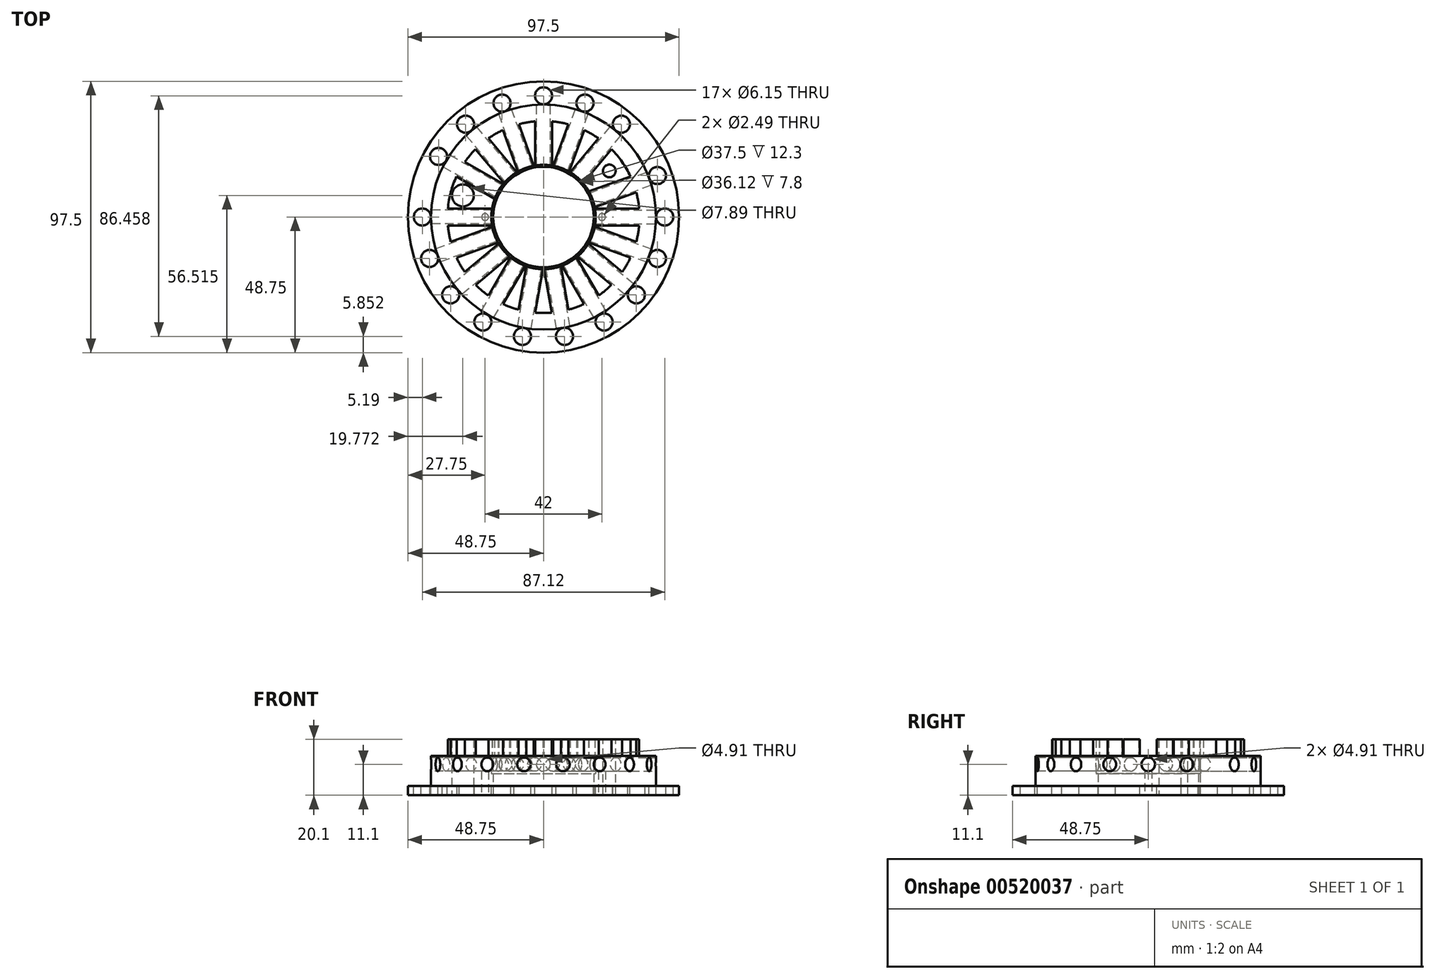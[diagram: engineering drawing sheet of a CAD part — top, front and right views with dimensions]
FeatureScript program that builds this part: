
annotation { "Feature Type Name" : "Feature", "Feature Type Description" : "" }
export const myFeature = defineFeature(function(context is Context, id is Id, definition is map)
    precondition{}
    {
        {
            var Q0;
            Q0=qCreatedBy(makeId("Front.planeOp"),FACE);
            var sketch = newSketch(context, id + "F0", { "sketchPlane" : qUnion([Q0])});
            skLineSegment(sketch, "E0", {"start": v(6.02, 0) * mm, "end": v(16.25, 0) * mm});
            skLineSegment(sketch, "E1", {"start": v(16.25, 0) * mm, "end": v(16.25, 1.1) * mm});
            skLineSegment(sketch, "E2", {"start": v(16.25, 1.1) * mm, "end": v(13.48, 1.1) * mm});
            skLineSegment(sketch, "E3", {"start": v(13.48, 1.1) * mm, "end": v(13.48, 4.7) * mm});
            skLineSegment(sketch, "E4", {"start": v(13.48, 4.7) * mm, "end": v(11.5, 4.7) * mm});
            skLineSegment(sketch, "E5", {"start": v(11.5, 4.7) * mm, "end": v(11.5, 6.7) * mm});
            skLineSegment(sketch, "E6", {"start": v(11.5, 6.7) * mm, "end": v(6.25, 6.7) * mm});
            skLineSegment(sketch, "E7", {"start": v(6.25, 6.7) * mm, "end": v(6.25, 2.6) * mm});
            skLineSegment(sketch, "E8", {"start": v(6.25, 2.6) * mm, "end": v(6.02, 2.6) * mm});
            skLineSegment(sketch, "E9", {"start": v(6.02, 2.6) * mm, "end": v(6.02, 0) * mm});
            skLineSegment(sketch, "E10", {"start": v(0, 0) * mm, "end": v(0, 6.7) * mm, "construction": true});
            skSolve(sketch);
        }
        {
            var Q0;
            Q0=makeQuery(id+"F0.imprint","IMPRINT",FACE,{"disambiguationData":[TD([[makeQuery(id+"F0.imprint","IMPRINT",EDGE,{"derivedFrom":sQuery(id+"F0.wireOp",EDGE,"E0")}),1.0]])]});
            var Q1;
            Q1=sQuery(id+"F0.wireOp",EDGE,"E10");
            revolve(context, id + "F1", {"entities" : qUnion([Q0]), "axis" : qUnion([Q1]), "revolveType" : RevolveType.FULL});
        }
        {
            var Q0;
            Q0=makeQuery(id+"F1.opRevolve","SWEPT_FACE",FACE,{"disambiguationData":[OSD([sQuery(id+"F0.wireOp",EDGE,"E6")])]});
            cPlane(context, id + "F2", {"entities" : qUnion([Q0]), "cplaneType" : CPlaneType.OFFSET, "offset" : 2 * mm, "oppositeDirection" : true, "width" : 150 * mm, "height" : 150 * mm});
        }
        {
            var Q0;
            Q0=qCreatedBy(id+"F2.planeOp",FACE);
            var sketch = newSketch(context, id + "F3", { "sketchPlane" : qUnion([Q0])});
            skLineSegment(sketch, "E11", {"start": v(-15, 1.01) * mm, "end": v(-15, -1.01) * mm});
            skLineSegment(sketch, "E12", {"start": v(-15, -1.01) * mm, "end": v(-5, -1.01) * mm});
            skLineSegment(sketch, "E13", {"start": v(-5, -1.01) * mm, "end": v(-5, 1.01) * mm});
            skLineSegment(sketch, "E14", {"start": v(-5, 1.01) * mm, "end": v(-15, 1.01) * mm});
            skPoint(sketch, "E15.center", {"position": v(0, 0) * mm});
            skLineSegment(sketch, "E16.1.0", {"start": v(-14.44, -4.18) * mm, "end": v(-13.75, -6.08) * mm});
            skLineSegment(sketch, "E16.1.1", {"start": v(-13.75, -6.08) * mm, "end": v(-4.35, -2.66) * mm});
            skLineSegment(sketch, "E16.1.2", {"start": v(-5.05, -0.76) * mm, "end": v(-14.44, -4.18) * mm});
            skLineSegment(sketch, "E16.1.3", {"start": v(-4.35, -2.66) * mm, "end": v(-5.05, -0.76) * mm});
            skLineSegment(sketch, "E16.2.0", {"start": v(-12.14, -8.87) * mm, "end": v(-10.84, -10.42) * mm});
            skLineSegment(sketch, "E16.2.1", {"start": v(-10.84, -10.42) * mm, "end": v(-3.18, -4) * mm});
            skLineSegment(sketch, "E16.2.2", {"start": v(-4.48, -2.44) * mm, "end": v(-12.14, -8.87) * mm});
            skLineSegment(sketch, "E16.2.3", {"start": v(-3.18, -4) * mm, "end": v(-4.48, -2.44) * mm});
            skLineSegment(sketch, "E16.3.0", {"start": v(-8.38, -12.48) * mm, "end": v(-6.62, -13.5) * mm});
            skLineSegment(sketch, "E16.3.1", {"start": v(-6.62, -13.5) * mm, "end": v(-1.62, -4.84) * mm});
            skLineSegment(sketch, "E16.3.2", {"start": v(-3.38, -3.82) * mm, "end": v(-8.38, -12.48) * mm});
            skLineSegment(sketch, "E16.3.3", {"start": v(-1.62, -4.84) * mm, "end": v(-3.38, -3.82) * mm});
            skLineSegment(sketch, "E16.4.0", {"start": v(-3.6, -14.6) * mm, "end": v(-1.6, -14.95) * mm});
            skLineSegment(sketch, "E16.4.1", {"start": v(-1.6, -14.95) * mm, "end": v(0.13, -5.1) * mm});
            skLineSegment(sketch, "E16.4.2", {"start": v(-1.87, -4.75) * mm, "end": v(-3.6, -14.6) * mm});
            skLineSegment(sketch, "E16.4.3", {"start": v(0.13, -5.1) * mm, "end": v(-1.87, -4.75) * mm});
            skLineSegment(sketch, "E16.5.0", {"start": v(1.6, -14.95) * mm, "end": v(3.6, -14.6) * mm});
            skLineSegment(sketch, "E16.5.1", {"start": v(3.6, -14.6) * mm, "end": v(1.87, -4.75) * mm});
            skLineSegment(sketch, "E16.5.2", {"start": v(-0.13, -5.1) * mm, "end": v(1.6, -14.95) * mm});
            skLineSegment(sketch, "E16.5.3", {"start": v(1.87, -4.75) * mm, "end": v(-0.13, -5.1) * mm});
            skLineSegment(sketch, "E16.6.0", {"start": v(6.62, -13.5) * mm, "end": v(8.38, -12.48) * mm});
            skLineSegment(sketch, "E16.6.1", {"start": v(8.38, -12.48) * mm, "end": v(3.38, -3.82) * mm});
            skLineSegment(sketch, "E16.6.2", {"start": v(1.62, -4.84) * mm, "end": v(6.62, -13.5) * mm});
            skLineSegment(sketch, "E16.6.3", {"start": v(3.38, -3.82) * mm, "end": v(1.62, -4.84) * mm});
            skLineSegment(sketch, "E16.7.0", {"start": v(10.84, -10.42) * mm, "end": v(12.14, -8.87) * mm});
            skLineSegment(sketch, "E16.7.1", {"start": v(12.14, -8.87) * mm, "end": v(4.48, -2.44) * mm});
            skLineSegment(sketch, "E16.7.2", {"start": v(3.18, -4) * mm, "end": v(10.84, -10.42) * mm});
            skLineSegment(sketch, "E16.7.3", {"start": v(4.48, -2.44) * mm, "end": v(3.18, -4) * mm});
            skLineSegment(sketch, "E16.8.0", {"start": v(13.75, -6.08) * mm, "end": v(14.44, -4.18) * mm});
            skLineSegment(sketch, "E16.8.1", {"start": v(14.44, -4.18) * mm, "end": v(5.05, -0.76) * mm});
            skLineSegment(sketch, "E16.8.2", {"start": v(4.35, -2.66) * mm, "end": v(13.75, -6.08) * mm});
            skLineSegment(sketch, "E16.8.3", {"start": v(5.05, -0.76) * mm, "end": v(4.35, -2.66) * mm});
            skLineSegment(sketch, "E16.9.0", {"start": v(15, -1.01) * mm, "end": v(15, 1.01) * mm});
            skLineSegment(sketch, "E16.9.1", {"start": v(15, 1.01) * mm, "end": v(5, 1.01) * mm});
            skLineSegment(sketch, "E16.9.2", {"start": v(5, -1.01) * mm, "end": v(15, -1.01) * mm});
            skLineSegment(sketch, "E16.9.3", {"start": v(5, 1.01) * mm, "end": v(5, -1.01) * mm});
            skLineSegment(sketch, "E16.10.0", {"start": v(14.44, 4.18) * mm, "end": v(13.75, 6.08) * mm});
            skLineSegment(sketch, "E16.10.1", {"start": v(13.75, 6.08) * mm, "end": v(4.35, 2.66) * mm});
            skLineSegment(sketch, "E16.10.2", {"start": v(5.05, 0.76) * mm, "end": v(14.44, 4.18) * mm});
            skLineSegment(sketch, "E16.10.3", {"start": v(4.35, 2.66) * mm, "end": v(5.05, 0.76) * mm});
            skLineSegment(sketch, "E16.anchor1", {"start": v(0, 0) * mm, "end": v(-15, -1.01) * mm, "construction": true});
            skLineSegment(sketch, "E16.anchor2", {"start": v(0, 0) * mm, "end": v(13.75, 6.08) * mm, "construction": true});
            skLineSegment(sketch, "E17", {"start": v(-13.5, 6.62) * mm, "end": v(-4.84, 1.62) * mm});
            skLineSegment(sketch, "E18", {"start": v(-4.84, 1.62) * mm, "end": v(-3.82, 3.38) * mm});
            skLineSegment(sketch, "E19", {"start": v(-3.82, 3.38) * mm, "end": v(-12.48, 8.38) * mm});
            skLineSegment(sketch, "E20", {"start": v(-12.48, 8.38) * mm, "end": v(-13.5, 6.62) * mm});
            skLineSegment(sketch, "E21", {"start": v(-13, 7.5) * mm, "end": v(-4.33, 2.5) * mm, "construction": true});
            skLineSegment(sketch, "E22.1.0", {"start": v(-8.87, 12.14) * mm, "end": v(-10.42, 10.84) * mm});
            skLineSegment(sketch, "E22.1.1", {"start": v(-10.42, 10.84) * mm, "end": v(-4, 3.18) * mm});
            skLineSegment(sketch, "E22.1.2", {"start": v(-2.44, 4.48) * mm, "end": v(-8.87, 12.14) * mm});
            skLineSegment(sketch, "E22.1.3", {"start": v(-4, 3.18) * mm, "end": v(-2.44, 4.48) * mm});
            skLineSegment(sketch, "E22.2.0", {"start": v(-4.18, 14.44) * mm, "end": v(-6.08, 13.75) * mm});
            skLineSegment(sketch, "E22.2.1", {"start": v(-6.08, 13.75) * mm, "end": v(-2.66, 4.35) * mm});
            skLineSegment(sketch, "E22.2.2", {"start": v(-0.76, 5.05) * mm, "end": v(-4.18, 14.44) * mm});
            skLineSegment(sketch, "E22.2.3", {"start": v(-2.66, 4.35) * mm, "end": v(-0.76, 5.05) * mm});
            skLineSegment(sketch, "E22.3.0", {"start": v(1.01, 15) * mm, "end": v(-1.01, 15) * mm});
            skLineSegment(sketch, "E22.3.1", {"start": v(-1.01, 15) * mm, "end": v(-1.01, 5) * mm});
            skLineSegment(sketch, "E22.3.2", {"start": v(1.01, 5) * mm, "end": v(1.01, 15) * mm});
            skLineSegment(sketch, "E22.3.3", {"start": v(-1.01, 5) * mm, "end": v(1.01, 5) * mm});
            skLineSegment(sketch, "E22.4.0", {"start": v(6.08, 13.75) * mm, "end": v(4.18, 14.44) * mm});
            skLineSegment(sketch, "E22.4.1", {"start": v(4.18, 14.44) * mm, "end": v(0.76, 5.05) * mm});
            skLineSegment(sketch, "E22.4.2", {"start": v(2.66, 4.35) * mm, "end": v(6.08, 13.75) * mm});
            skLineSegment(sketch, "E22.4.3", {"start": v(0.76, 5.05) * mm, "end": v(2.66, 4.35) * mm});
            skLineSegment(sketch, "E22.5.0", {"start": v(10.42, 10.84) * mm, "end": v(8.87, 12.14) * mm});
            skLineSegment(sketch, "E22.5.1", {"start": v(8.87, 12.14) * mm, "end": v(2.44, 4.48) * mm});
            skLineSegment(sketch, "E22.5.2", {"start": v(4, 3.18) * mm, "end": v(10.42, 10.84) * mm});
            skLineSegment(sketch, "E22.5.3", {"start": v(2.44, 4.48) * mm, "end": v(4, 3.18) * mm});
            skLineSegment(sketch, "E22.anchor1", {"start": v(0, 0) * mm, "end": v(-13.5, 6.62) * mm, "construction": true});
            skLineSegment(sketch, "E22.anchor2", {"start": v(0, 0) * mm, "end": v(8.87, 12.14) * mm, "construction": true});
            skSolve(sketch);
        }
        {
            var Q0;
            Q0=qSketchRegion(id+"F3",true);
            extrude(context, id + "F4", {"entities" : qUnion([Q0]), "operationType" : NewBodyOperationType.REMOVE, "endBound" : BoundingType.THROUGH_ALL, "depth" : 25 * mm});
        }
        {
            var Q0;
            Q0=makeQuery(id+"F1.opRevolve","SWEPT_FACE",FACE,{"disambiguationData":[OSD([sQuery(id+"F0.wireOp",EDGE,"E2")])]});
            var sketch = newSketch(context, id + "F5", { "sketchPlane" : qUnion([Q0])});
            skCircle(sketch, "E23", {"center": v(0, 0) * mm, "radius": 14.52 * mm, "construction": true});
            skCircle(sketch, "E24", {"center": v(-14.52, 0) * mm, "radius": 1.02 * mm});
            skLineSegment(sketch, "E25.anchor1", {"start": v(0, 0) * mm, "end": v(-14.52, 0) * mm, "construction": true});
            skCircle(sketch, "E26.1.0", {"center": v(-12.57, 7.26) * mm, "radius": 1.02 * mm});
            skLineSegment(sketch, "E26.anchor2", {"start": v(0, 0) * mm, "end": v(-12.57, 7.26) * mm, "construction": true});
            skCircle(sketch, "E27.1.0", {"center": v(-13.64, -4.97) * mm, "radius": 1.02 * mm});
            skCircle(sketch, "E27.2.0", {"center": v(-11.12, -9.33) * mm, "radius": 1.02 * mm});
            skCircle(sketch, "E27.3.0", {"center": v(-7.26, -12.57) * mm, "radius": 1.02 * mm});
            skCircle(sketch, "E27.4.0", {"center": v(-2.52, -14.3) * mm, "radius": 1.02 * mm});
            skCircle(sketch, "E27.5.0", {"center": v(2.52, -14.3) * mm, "radius": 1.02 * mm});
            skCircle(sketch, "E27.6.0", {"center": v(7.26, -12.57) * mm, "radius": 1.02 * mm});
            skCircle(sketch, "E27.7.0", {"center": v(11.12, -9.33) * mm, "radius": 1.02 * mm});
            skCircle(sketch, "E27.8.0", {"center": v(13.64, -4.97) * mm, "radius": 1.02 * mm});
            skCircle(sketch, "E27.9.0", {"center": v(14.52, 0) * mm, "radius": 1.02 * mm});
            skCircle(sketch, "E27.10.0", {"center": v(13.64, 4.97) * mm, "radius": 1.02 * mm});
            skLineSegment(sketch, "E27.anchor2", {"start": v(0, 0) * mm, "end": v(13.64, 4.97) * mm, "construction": true});
            skCircle(sketch, "E28.1.0", {"center": v(-9.33, 11.12) * mm, "radius": 1.02 * mm});
            skCircle(sketch, "E28.2.0", {"center": v(-4.97, 13.64) * mm, "radius": 1.02 * mm});
            skCircle(sketch, "E28.3.0", {"center": v(0, 14.52) * mm, "radius": 1.02 * mm});
            skCircle(sketch, "E28.4.0", {"center": v(4.97, 13.64) * mm, "radius": 1.02 * mm});
            skCircle(sketch, "E28.5.0", {"center": v(9.33, 11.12) * mm, "radius": 1.02 * mm});
            skLineSegment(sketch, "E28.anchor2", {"start": v(0, 0) * mm, "end": v(9.33, 11.12) * mm, "construction": true});
            skSolve(sketch);
        }
        {
            var Q0;
            Q0=qSketchRegion(id+"F5",true);
            extrude(context, id + "F6", {"entities" : qUnion([Q0]), "operationType" : NewBodyOperationType.REMOVE, "endBound" : BoundingType.THROUGH_ALL, "oppositeDirection" : true, "depth" : 25 * mm});
        }
        {
            var Q0;
            Q0=makeQuery(id+"F1.opRevolve","SWEPT_FACE",FACE,{"disambiguationData":[OSD([sQuery(id+"F0.wireOp",EDGE,"E0")])]});
            var sketch = newSketch(context, id + "F7", { "sketchPlane" : qUnion([Q0])});
            skCircle(sketch, "E29", {"center": v(-9.66, -2.59) * mm, "radius": 1.31 * mm});
            skLineSegment(sketch, "E30", {"start": v(-9.66, -2.59) * mm, "end": v(0, 0) * mm, "construction": true});
            skSolve(sketch);
        }
        {
            var Q0;
            Q0=makeQuery(id+"F7.imprint","IMPRINT",FACE,{"disambiguationData":[TD([[makeQuery(id+"F7.imprint","IMPRINT",EDGE,{"derivedFrom":sQuery(id+"F7.wireOp",EDGE,"E29")}),1.0]])]});
            extrude(context, id + "F8", {"entities" : qUnion([Q0]), "operationType" : NewBodyOperationType.REMOVE, "endBound" : BoundingType.THROUGH_ALL, "oppositeDirection" : true, "depth" : 25 * mm});
        }
        {
            var Q0;
            Q0=makeQuery(id+"F4.boolean.opBoolean","SPLIT",FACE,{"disambiguationData":[TD([makeQuery(id+"F4.opExtrude","SWEPT_FACE",FACE,{"disambiguationData":[OSD([sQuery(id+"F3.wireOp",EDGE,"E16.10.2")])]})])],"derivedFrom":makeQuery(id+"F1.opRevolve","SWEPT_FACE",FACE,{"disambiguationData":[OSD([sQuery(id+"F0.wireOp",EDGE,"E6")])]})});
            var sketch = newSketch(context, id + "F9", { "sketchPlane" : qUnion([Q0])});
            skCircle(sketch, "E31", {"center": v(7.88, 5.52) * mm, "radius": 0.76 * mm});
            skLineSegment(sketch, "E32", {"start": v(7.88, 5.52) * mm, "end": v(0, 0) * mm, "construction": true});
            skSolve(sketch);
        }
        {
            var Q0;
            Q0=makeQuery(id+"F9.imprint","IMPRINT",FACE,{"disambiguationData":[TD([[makeQuery(id+"F9.imprint","IMPRINT",EDGE,{"derivedFrom":sQuery(id+"F9.wireOp",EDGE,"E31")}),1.0]])]});
            var Q2;
            Q2=makeQuery(id+"F1.opRevolve","SWEPT_FACE",FACE,{"disambiguationData":[OSD([sQuery(id+"F0.wireOp",EDGE,"E0")])]});
            extrude(context, id + "F10", {"entities" : qUnion([Q0]), "operationType" : NewBodyOperationType.REMOVE, "endBound" : BoundingType.UP_TO_SURFACE, "oppositeDirection" : true, "depth" : 1.3 * mm, "endBoundEntityFace" : qUnion([Q2])});
        }
        {
            var Q0;
            Q0=makeQuery(id+"F1.opRevolve","SWEPT_FACE",FACE,{"disambiguationData":[OSD([sQuery(id+"F0.wireOp",EDGE,"E0")])]});
            var sketch = newSketch(context, id + "F11", { "sketchPlane" : qUnion([Q0])});
            skCircle(sketch, "E33", {"center": v(0, 0) * mm, "radius": 7 * mm, "construction": true});
            skCircle(sketch, "E34", {"center": v(-7, 0) * mm, "radius": 0.41 * mm});
            skCircle(sketch, "E35", {"center": v(7, 0) * mm, "radius": 0.41 * mm});
            skSolve(sketch);
        }
        {
            var Q0;
            {Q0=qUnion([makeQuery(id+"F11.imprint","IMPRINT",FACE,{"disambiguationData":[TD([[makeQuery(id+"F11.imprint","IMPRINT",EDGE,{"derivedFrom":sQuery(id+"F11.wireOp",EDGE,"E34")}),1.0]])]}),makeQuery(id+"F11.imprint","IMPRINT",FACE,{"disambiguationData":[TD([[makeQuery(id+"F11.imprint","IMPRINT",EDGE,{"derivedFrom":sQuery(id+"F11.wireOp",EDGE,"E35")}),1.0]])]})]);}
            extrude(context, id + "F12", {"entities" : qUnion([Q0]), "operationType" : NewBodyOperationType.REMOVE, "oppositeDirection" : true, "depth" : 3.7 * mm});
        }
        {
            var Q0;
            Q0=qCreatedBy(id+"F2.planeOp",FACE);
            cPlane(context, id + "F13", {"entities" : qUnion([Q0]), "cplaneType" : CPlaneType.OFFSET, "offset" : 1 * mm, "oppositeDirection" : true, "width" : 150 * mm, "height" : 150 * mm});
        }
        {
            var Q0;
            Q0=qCreatedBy(id+"F13.planeOp",FACE);
            var sketch = newSketch(context, id + "F14", { "sketchPlane" : qUnion([Q0])});
            skLineSegment(sketch, "E36.bottom", {"start": v(-17.2, 0.82) * mm, "end": v(-6.2, 0.82) * mm});
            skLineSegment(sketch, "E36.top", {"start": v(-17.2, 0) * mm, "end": v(-6.2, 0) * mm});
            skLineSegment(sketch, "E36.left", {"start": v(-17.2, 0.82) * mm, "end": v(-17.2, 0) * mm});
            skLineSegment(sketch, "E36.right", {"start": v(-6.2, 0.82) * mm, "end": v(-6.2, 0) * mm});
            skSolve(sketch);
        }
        {
            var Q0;
            Q0=makeQuery(id+"F14.imprint","IMPRINT",FACE,{"disambiguationData":[TD([[makeQuery(id+"F14.imprint","IMPRINT",EDGE,{"derivedFrom":sQuery(id+"F14.wireOp",EDGE,"E36.bottom")}),-1.0]])]});
            var Q1;
            Q1=sQuery(id+"F14.wireOp",EDGE,"E36.top");
            revolve(context, id + "F15", {"entities" : qUnion([Q0]), "axis" : qUnion([Q1]), "revolveType" : RevolveType.FULL});
        }
        {
            var Q0;
            Q0=makeQuery(id+"F15.opRevolve","SWEPT_BODY",BODY,{"disambiguationData":[OSD([sQuery(id+"F14.wireOp",EDGE,"E36.bottom"),sQuery(id+"F14.wireOp",EDGE,"E36.top"),sQuery(id+"F14.wireOp",EDGE,"E36.left"),sQuery(id+"F14.wireOp",EDGE,"E36.right")])]});
            var Q1;
            Q1=sQuery(id+"F0.wireOp",EDGE,"E10");
            circularPattern(context, id + "F16", {"entities" : qUnion([Q0]), "axis" : qUnion([Q1]), "angle" : 20 * degree, "instanceCount" : round(11)});
        }
        {
            var Q0;
            Q0=makeQuery(id+"F15.opRevolve","SWEPT_BODY",BODY,{"disambiguationData":[OSD([sQuery(id+"F14.wireOp",EDGE,"E36.bottom"),sQuery(id+"F14.wireOp",EDGE,"E36.top"),sQuery(id+"F14.wireOp",EDGE,"E36.left"),sQuery(id+"F14.wireOp",EDGE,"E36.right")])]});
            var Q1;
            Q1=sQuery(id+"F0.wireOp",EDGE,"E10");
            transform(context, id + "F17", {"entities" : qUnion([Q0]), "transformType" : TransformType.ROTATION, "transformAxis" : qUnion([Q1]), "angle" : 30 * degree, "oppositeDirection" : true, "makeCopy" : true});
        }
        {
            var Q0;
            Q0=makeQuery(id+"F17.opPattern","COPY",FACE,{"derivedFrom":makeQuery(id+"F15.opRevolve","SWEPT_FACE",FACE,{"disambiguationData":[OSD([sQuery(id+"F14.wireOp",EDGE,"E36.bottom")])]}),"instanceName":"1"});
            var Q1;
            Q1=makeQuery(id+"F17.opPattern","COPY",BODY,{"derivedFrom":makeQuery(id+"F15.opRevolve","SWEPT_BODY",BODY,{"disambiguationData":[OSD([sQuery(id+"F14.wireOp",EDGE,"E36.bottom"),sQuery(id+"F14.wireOp",EDGE,"E36.top"),sQuery(id+"F14.wireOp",EDGE,"E36.left"),sQuery(id+"F14.wireOp",EDGE,"E36.right")])]}),"instanceName":"1"});
            var Q2;
            Q2=sQuery(id+"F0.wireOp",EDGE,"E10");
            circularPattern(context, id + "F18", {"entities" : qUnion([Q1]), "axis" : qUnion([Q2]), "angle" : 20 * degree, "instanceCount" : round(6), "oppositeDirection" : true});
        }
        {
            var Q0;
            Q0=makeQuery(id+"F15.opRevolve","SWEPT_BODY",BODY,{"disambiguationData":[OSD([sQuery(id+"F14.wireOp",EDGE,"E36.bottom"),sQuery(id+"F14.wireOp",EDGE,"E36.top"),sQuery(id+"F14.wireOp",EDGE,"E36.left"),sQuery(id+"F14.wireOp",EDGE,"E36.right")])]});
            var Q1;
            Q1=makeQuery(id+"F16.opPattern","COPY",BODY,{"derivedFrom":makeQuery(id+"F15.opRevolve","SWEPT_BODY",BODY,{"disambiguationData":[OSD([sQuery(id+"F14.wireOp",EDGE,"E36.bottom"),sQuery(id+"F14.wireOp",EDGE,"E36.top"),sQuery(id+"F14.wireOp",EDGE,"E36.left"),sQuery(id+"F14.wireOp",EDGE,"E36.right")])]}),"instanceName":"1"});
            var Q2;
            Q2=makeQuery(id+"F16.opPattern","COPY",BODY,{"derivedFrom":makeQuery(id+"F15.opRevolve","SWEPT_BODY",BODY,{"disambiguationData":[OSD([sQuery(id+"F14.wireOp",EDGE,"E36.bottom"),sQuery(id+"F14.wireOp",EDGE,"E36.top"),sQuery(id+"F14.wireOp",EDGE,"E36.left"),sQuery(id+"F14.wireOp",EDGE,"E36.right")])]}),"instanceName":"2"});
            var Q3;
            Q3=makeQuery(id+"F16.opPattern","COPY",BODY,{"derivedFrom":makeQuery(id+"F15.opRevolve","SWEPT_BODY",BODY,{"disambiguationData":[OSD([sQuery(id+"F14.wireOp",EDGE,"E36.bottom"),sQuery(id+"F14.wireOp",EDGE,"E36.top"),sQuery(id+"F14.wireOp",EDGE,"E36.left"),sQuery(id+"F14.wireOp",EDGE,"E36.right")])]}),"instanceName":"3"});
            var Q4;
            Q4=makeQuery(id+"F16.opPattern","COPY",BODY,{"derivedFrom":makeQuery(id+"F15.opRevolve","SWEPT_BODY",BODY,{"disambiguationData":[OSD([sQuery(id+"F14.wireOp",EDGE,"E36.bottom"),sQuery(id+"F14.wireOp",EDGE,"E36.top"),sQuery(id+"F14.wireOp",EDGE,"E36.left"),sQuery(id+"F14.wireOp",EDGE,"E36.right")])]}),"instanceName":"4"});
            var Q5;
            Q5=makeQuery(id+"F16.opPattern","COPY",BODY,{"derivedFrom":makeQuery(id+"F15.opRevolve","SWEPT_BODY",BODY,{"disambiguationData":[OSD([sQuery(id+"F14.wireOp",EDGE,"E36.bottom"),sQuery(id+"F14.wireOp",EDGE,"E36.top"),sQuery(id+"F14.wireOp",EDGE,"E36.left"),sQuery(id+"F14.wireOp",EDGE,"E36.right")])]}),"instanceName":"5"});
            var Q6;
            Q6=makeQuery(id+"F16.opPattern","COPY",BODY,{"derivedFrom":makeQuery(id+"F15.opRevolve","SWEPT_BODY",BODY,{"disambiguationData":[OSD([sQuery(id+"F14.wireOp",EDGE,"E36.bottom"),sQuery(id+"F14.wireOp",EDGE,"E36.top"),sQuery(id+"F14.wireOp",EDGE,"E36.left"),sQuery(id+"F14.wireOp",EDGE,"E36.right")])]}),"instanceName":"6"});
            var Q7;
            Q7=makeQuery(id+"F16.opPattern","COPY",BODY,{"derivedFrom":makeQuery(id+"F15.opRevolve","SWEPT_BODY",BODY,{"disambiguationData":[OSD([sQuery(id+"F14.wireOp",EDGE,"E36.bottom"),sQuery(id+"F14.wireOp",EDGE,"E36.top"),sQuery(id+"F14.wireOp",EDGE,"E36.left"),sQuery(id+"F14.wireOp",EDGE,"E36.right")])]}),"instanceName":"7"});
            var Q8;
            Q8=makeQuery(id+"F16.opPattern","COPY",BODY,{"derivedFrom":makeQuery(id+"F15.opRevolve","SWEPT_BODY",BODY,{"disambiguationData":[OSD([sQuery(id+"F14.wireOp",EDGE,"E36.bottom"),sQuery(id+"F14.wireOp",EDGE,"E36.top"),sQuery(id+"F14.wireOp",EDGE,"E36.left"),sQuery(id+"F14.wireOp",EDGE,"E36.right")])]}),"instanceName":"8"});
            var Q9;
            Q9=makeQuery(id+"F16.opPattern","COPY",BODY,{"derivedFrom":makeQuery(id+"F15.opRevolve","SWEPT_BODY",BODY,{"disambiguationData":[OSD([sQuery(id+"F14.wireOp",EDGE,"E36.bottom"),sQuery(id+"F14.wireOp",EDGE,"E36.top"),sQuery(id+"F14.wireOp",EDGE,"E36.left"),sQuery(id+"F14.wireOp",EDGE,"E36.right")])]}),"instanceName":"9"});
            var Q10;
            Q10=makeQuery(id+"F16.opPattern","COPY",BODY,{"derivedFrom":makeQuery(id+"F15.opRevolve","SWEPT_BODY",BODY,{"disambiguationData":[OSD([sQuery(id+"F14.wireOp",EDGE,"E36.bottom"),sQuery(id+"F14.wireOp",EDGE,"E36.top"),sQuery(id+"F14.wireOp",EDGE,"E36.left"),sQuery(id+"F14.wireOp",EDGE,"E36.right")])]}),"instanceName":"10"});
            var Q11;
            Q11=makeQuery(id+"F17.opPattern","COPY",BODY,{"derivedFrom":makeQuery(id+"F15.opRevolve","SWEPT_BODY",BODY,{"disambiguationData":[OSD([sQuery(id+"F14.wireOp",EDGE,"E36.bottom"),sQuery(id+"F14.wireOp",EDGE,"E36.top"),sQuery(id+"F14.wireOp",EDGE,"E36.left"),sQuery(id+"F14.wireOp",EDGE,"E36.right")])]}),"instanceName":"1"});
            var Q12;
            Q12=makeQuery(id+"F18.opPattern","COPY",BODY,{"derivedFrom":makeQuery(id+"F17.opPattern","COPY",BODY,{"derivedFrom":makeQuery(id+"F15.opRevolve","SWEPT_BODY",BODY,{"disambiguationData":[OSD([sQuery(id+"F14.wireOp",EDGE,"E36.bottom"),sQuery(id+"F14.wireOp",EDGE,"E36.top"),sQuery(id+"F14.wireOp",EDGE,"E36.left"),sQuery(id+"F14.wireOp",EDGE,"E36.right")])]}),"instanceName":"1"}),"instanceName":"1"});
            var Q13;
            Q13=makeQuery(id+"F18.opPattern","COPY",BODY,{"derivedFrom":makeQuery(id+"F17.opPattern","COPY",BODY,{"derivedFrom":makeQuery(id+"F15.opRevolve","SWEPT_BODY",BODY,{"disambiguationData":[OSD([sQuery(id+"F14.wireOp",EDGE,"E36.bottom"),sQuery(id+"F14.wireOp",EDGE,"E36.top"),sQuery(id+"F14.wireOp",EDGE,"E36.left"),sQuery(id+"F14.wireOp",EDGE,"E36.right")])]}),"instanceName":"1"}),"instanceName":"2"});
            var Q14;
            Q14=makeQuery(id+"F18.opPattern","COPY",BODY,{"derivedFrom":makeQuery(id+"F17.opPattern","COPY",BODY,{"derivedFrom":makeQuery(id+"F15.opRevolve","SWEPT_BODY",BODY,{"disambiguationData":[OSD([sQuery(id+"F14.wireOp",EDGE,"E36.bottom"),sQuery(id+"F14.wireOp",EDGE,"E36.top"),sQuery(id+"F14.wireOp",EDGE,"E36.left"),sQuery(id+"F14.wireOp",EDGE,"E36.right")])]}),"instanceName":"1"}),"instanceName":"3"});
            var Q15;
            Q15=makeQuery(id+"F18.opPattern","COPY",BODY,{"derivedFrom":makeQuery(id+"F17.opPattern","COPY",BODY,{"derivedFrom":makeQuery(id+"F15.opRevolve","SWEPT_BODY",BODY,{"disambiguationData":[OSD([sQuery(id+"F14.wireOp",EDGE,"E36.bottom"),sQuery(id+"F14.wireOp",EDGE,"E36.top"),sQuery(id+"F14.wireOp",EDGE,"E36.left"),sQuery(id+"F14.wireOp",EDGE,"E36.right")])]}),"instanceName":"1"}),"instanceName":"4"});
            var Q16;
            Q16=makeQuery(id+"F18.opPattern","COPY",BODY,{"derivedFrom":makeQuery(id+"F17.opPattern","COPY",BODY,{"derivedFrom":makeQuery(id+"F15.opRevolve","SWEPT_BODY",BODY,{"disambiguationData":[OSD([sQuery(id+"F14.wireOp",EDGE,"E36.bottom"),sQuery(id+"F14.wireOp",EDGE,"E36.top"),sQuery(id+"F14.wireOp",EDGE,"E36.left"),sQuery(id+"F14.wireOp",EDGE,"E36.right")])]}),"instanceName":"1"}),"instanceName":"5"});
            var Q17;
            Q17=makeQuery(id+"F1.opRevolve","SWEPT_BODY",BODY,{"disambiguationData":[OSD([sQuery(id+"F0.wireOp",EDGE,"E0"),sQuery(id+"F0.wireOp",EDGE,"E1"),sQuery(id+"F0.wireOp",EDGE,"E2"),sQuery(id+"F0.wireOp",EDGE,"E3"),sQuery(id+"F0.wireOp",EDGE,"E4"),sQuery(id+"F0.wireOp",EDGE,"E5"),sQuery(id+"F0.wireOp",EDGE,"E6"),sQuery(id+"F0.wireOp",EDGE,"E7"),sQuery(id+"F0.wireOp",EDGE,"E8"),sQuery(id+"F0.wireOp",EDGE,"E9")])]});
            booleanBodies(context, id + "F19", {"operationType" : BooleanOperationType.SUBTRACTION, "tools" : qUnion([Q0, Q1, Q2, Q3, Q4, Q5, Q6, Q7, Q8, Q9, Q10, Q11, Q12, Q13, Q14, Q15, Q16]), "targets" : qUnion([Q17])});
        }
        {
            var Q0;
            Q0=makeQuery(id+"F4.boolean.opBoolean","MERGE",FACE,{"derivedFrom":[makeQuery(id+"F1.opRevolve","SWEPT_FACE",FACE,{"disambiguationData":[OSD([sQuery(id+"F0.wireOp",EDGE,"E4")])]}),makeQuery(id+"F4.opExtrude","CAP_FACE",FACE,{"disambiguationData":[OSD([sQuery(id+"F3.wireOp",EDGE,"E11"),sQuery(id+"F3.wireOp",EDGE,"E12"),sQuery(id+"F3.wireOp",EDGE,"E13"),sQuery(id+"F3.wireOp",EDGE,"E14"),sQuery(id+"F3.wireOp",EDGE,"E16.1.0"),sQuery(id+"F3.wireOp",EDGE,"E16.1.1"),sQuery(id+"F3.wireOp",EDGE,"E16.1.2"),sQuery(id+"F3.wireOp",EDGE,"E16.1.3"),sQuery(id+"F3.wireOp",EDGE,"E16.2.0"),sQuery(id+"F3.wireOp",EDGE,"E16.2.1"),sQuery(id+"F3.wireOp",EDGE,"E16.2.2"),sQuery(id+"F3.wireOp",EDGE,"E16.2.3"),sQuery(id+"F3.wireOp",EDGE,"E16.3.0"),sQuery(id+"F3.wireOp",EDGE,"E16.3.1"),sQuery(id+"F3.wireOp",EDGE,"E16.3.2"),sQuery(id+"F3.wireOp",EDGE,"E16.3.3"),sQuery(id+"F3.wireOp",EDGE,"E16.4.0"),sQuery(id+"F3.wireOp",EDGE,"E16.4.1"),sQuery(id+"F3.wireOp",EDGE,"E16.4.2"),sQuery(id+"F3.wireOp",EDGE,"E16.4.3"),sQuery(id+"F3.wireOp",EDGE,"E16.5.0"),sQuery(id+"F3.wireOp",EDGE,"E16.5.1"),sQuery(id+"F3.wireOp",EDGE,"E16.5.2"),sQuery(id+"F3.wireOp",EDGE,"E16.5.3"),sQuery(id+"F3.wireOp",EDGE,"E16.6.0"),sQuery(id+"F3.wireOp",EDGE,"E16.6.1"),sQuery(id+"F3.wireOp",EDGE,"E16.6.2"),sQuery(id+"F3.wireOp",EDGE,"E16.6.3"),sQuery(id+"F3.wireOp",EDGE,"E16.7.0"),sQuery(id+"F3.wireOp",EDGE,"E16.7.1"),sQuery(id+"F3.wireOp",EDGE,"E16.7.2"),sQuery(id+"F3.wireOp",EDGE,"E16.7.3"),sQuery(id+"F3.wireOp",EDGE,"E16.8.0"),sQuery(id+"F3.wireOp",EDGE,"E16.8.1"),sQuery(id+"F3.wireOp",EDGE,"E16.8.2"),sQuery(id+"F3.wireOp",EDGE,"E16.8.3"),sQuery(id+"F3.wireOp",EDGE,"E16.9.0"),sQuery(id+"F3.wireOp",EDGE,"E16.9.1"),sQuery(id+"F3.wireOp",EDGE,"E16.9.2"),sQuery(id+"F3.wireOp",EDGE,"E16.9.3"),sQuery(id+"F3.wireOp",EDGE,"E16.10.0"),sQuery(id+"F3.wireOp",EDGE,"E16.10.1"),sQuery(id+"F3.wireOp",EDGE,"E16.10.2"),sQuery(id+"F3.wireOp",EDGE,"E16.10.3")])],"isStart":true}),makeQuery(id+"F4.opExtrude","CAP_FACE",FACE,{"disambiguationData":[OSD([sQuery(id+"F3.wireOp",EDGE,"E17"),sQuery(id+"F3.wireOp",EDGE,"E18"),sQuery(id+"F3.wireOp",EDGE,"E19"),sQuery(id+"F3.wireOp",EDGE,"E20"),sQuery(id+"F3.wireOp",EDGE,"E22.1.0"),sQuery(id+"F3.wireOp",EDGE,"E22.1.1"),sQuery(id+"F3.wireOp",EDGE,"E22.1.2"),sQuery(id+"F3.wireOp",EDGE,"E22.1.3"),sQuery(id+"F3.wireOp",EDGE,"E22.2.0"),sQuery(id+"F3.wireOp",EDGE,"E22.2.1"),sQuery(id+"F3.wireOp",EDGE,"E22.2.2"),sQuery(id+"F3.wireOp",EDGE,"E22.2.3"),sQuery(id+"F3.wireOp",EDGE,"E22.3.0"),sQuery(id+"F3.wireOp",EDGE,"E22.3.1"),sQuery(id+"F3.wireOp",EDGE,"E22.3.2"),sQuery(id+"F3.wireOp",EDGE,"E22.3.3"),sQuery(id+"F3.wireOp",EDGE,"E22.4.0"),sQuery(id+"F3.wireOp",EDGE,"E22.4.1"),sQuery(id+"F3.wireOp",EDGE,"E22.4.2"),sQuery(id+"F3.wireOp",EDGE,"E22.4.3"),sQuery(id+"F3.wireOp",EDGE,"E22.5.0"),sQuery(id+"F3.wireOp",EDGE,"E22.5.1"),sQuery(id+"F3.wireOp",EDGE,"E22.5.2"),sQuery(id+"F3.wireOp",EDGE,"E22.5.3")])],"isStart":true})]});
            cPlane(context, id + "F20", {"entities" : qUnion([Q0]), "cplaneType" : CPlaneType.OFFSET, "offset" : 4 * mm, "oppositeDirection" : true, "width" : 150 * mm, "height" : 150 * mm});
        }
        {
            var Q0;
            Q0=qCreatedBy(id+"F20.planeOp",FACE);
            var sketch = newSketch(context, id + "F21", { "sketchPlane" : qUnion([Q0])});
            skCircle(sketch, "E37", {"center": v(0, 0) * mm, "radius": 24.5 * mm});
            skCircle(sketch, "E38", {"center": v(0, 0) * mm, "radius": 23.9 * mm});
            skSolve(sketch);
        }
        {
            var Q0;
            Q0=makeQuery(id+"F21.imprint","IMPRINT",FACE,{"disambiguationData":[TD([[makeQuery(id+"F21.imprint","IMPRINT",EDGE,{"derivedFrom":sQuery(id+"F21.wireOp",EDGE,"E37")}),1.0]])]});
            extrude(context, id + "F22", {"entities" : qUnion([Q0]), "operationType" : NewBodyOperationType.REMOVE, "depth" : 0.7 * mm});
        }
        {
            var Q0;
            Q0=makeQuery(id+"F1.opRevolve","SWEPT_BODY",BODY,{"disambiguationData":[OSD([sQuery(id+"F0.wireOp",EDGE,"E0"),sQuery(id+"F0.wireOp",EDGE,"E1"),sQuery(id+"F0.wireOp",EDGE,"E2"),sQuery(id+"F0.wireOp",EDGE,"E3"),sQuery(id+"F0.wireOp",EDGE,"E4"),sQuery(id+"F0.wireOp",EDGE,"E5"),sQuery(id+"F0.wireOp",EDGE,"E6"),sQuery(id+"F0.wireOp",EDGE,"E7"),sQuery(id+"F0.wireOp",EDGE,"E8"),sQuery(id+"F0.wireOp",EDGE,"E9")])]});
            var Q1;
            Q1=qCreatedBy(makeId("Origin.pointOp"),VERTEX);
            transform(context, id + "F23", {"entities" : qUnion([Q0]), "transformType" : TransformType.SCALE_UNIFORMLY, "scale" : 3, "makeCopy" : false, "scalePoint" : qUnion([Q1])});
        }
    });
